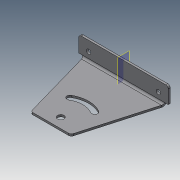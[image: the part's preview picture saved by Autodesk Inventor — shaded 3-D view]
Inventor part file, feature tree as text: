
AUTODESK INVENTOR PART (.ipt)
format: ipt  version: 2015 (Build 190159000, 159)  size: 190,464 bytes
history: native  units: mm
features: sheet_metal_op x6, other x5, plane x2, sketch x2, hole x1, mirror x1, chamfer x1
ambient origin geometry x8: Origin, YZ Plane, XZ Plane, XY Plane, X Axis, Y Axis, Z Axis, Center Point
bodies: Solid1 (feature_tree)
feature tree (18):
  sheet_metal_op  "Face1"
  sheet_metal_op  "Flange1"
  sheet_metal_op  "Flange2"
  hole  "Hole2"  [1 undecoded]
  plane  "Work Plane1"
  mirror  "Mirror1"
  chamfer  "Corner Round2"
  other  "A-Side Definition"
  other  "Plate1"
  other  "Plate2"
  sheet_metal_op  "Bend1"
  plane  "Work Plane2"
  sketch  "Sketch5"  dims[d2=165.0mm d3=80.0mm]
  sketch  "Sketch6"  dims[d4=150.0mm d5=42.5mm d6=3.9mm d23=0.0mm d24=0.0mm d25=4.0mm d26=2.0mm d27=8.0mm d28=3.9mm d29=36.0mm d30=90.0deg d31=3.9mm d68=20.0mm d69=20.0mm d34=9.0mm d35=6.0mm d36=4.0mm d37=2.0mm d38=90.0deg d39=4.0mm d40=20.594885mm d44=20.0mm d45=40.0mm d46=13.0mm d47=12.0mm d48=50.0mm d51=12.0mm d52=50.0mm d53=50.0mm d54=25.0mm d55=4.0mm d56=0.0mm d57=5.0mm d58=4.0mm d59=2.0mm d60=8.0mm d61=3.9mm d62=7.5mm d63=0.0mm d64=3.9mm d65=16.0mm d66=4.0mm d67=3.9mm]
  other  "Plate3"
  sheet_metal_op  "Bend2"
  sheet_metal_op  "Corner1"
  other  "Cut1"
note: 1 required parameter value undecoded (feature->parameter linkage not recoverable at this tier; creation-order binding heuristic only, values carry confidence <= 0.55)
